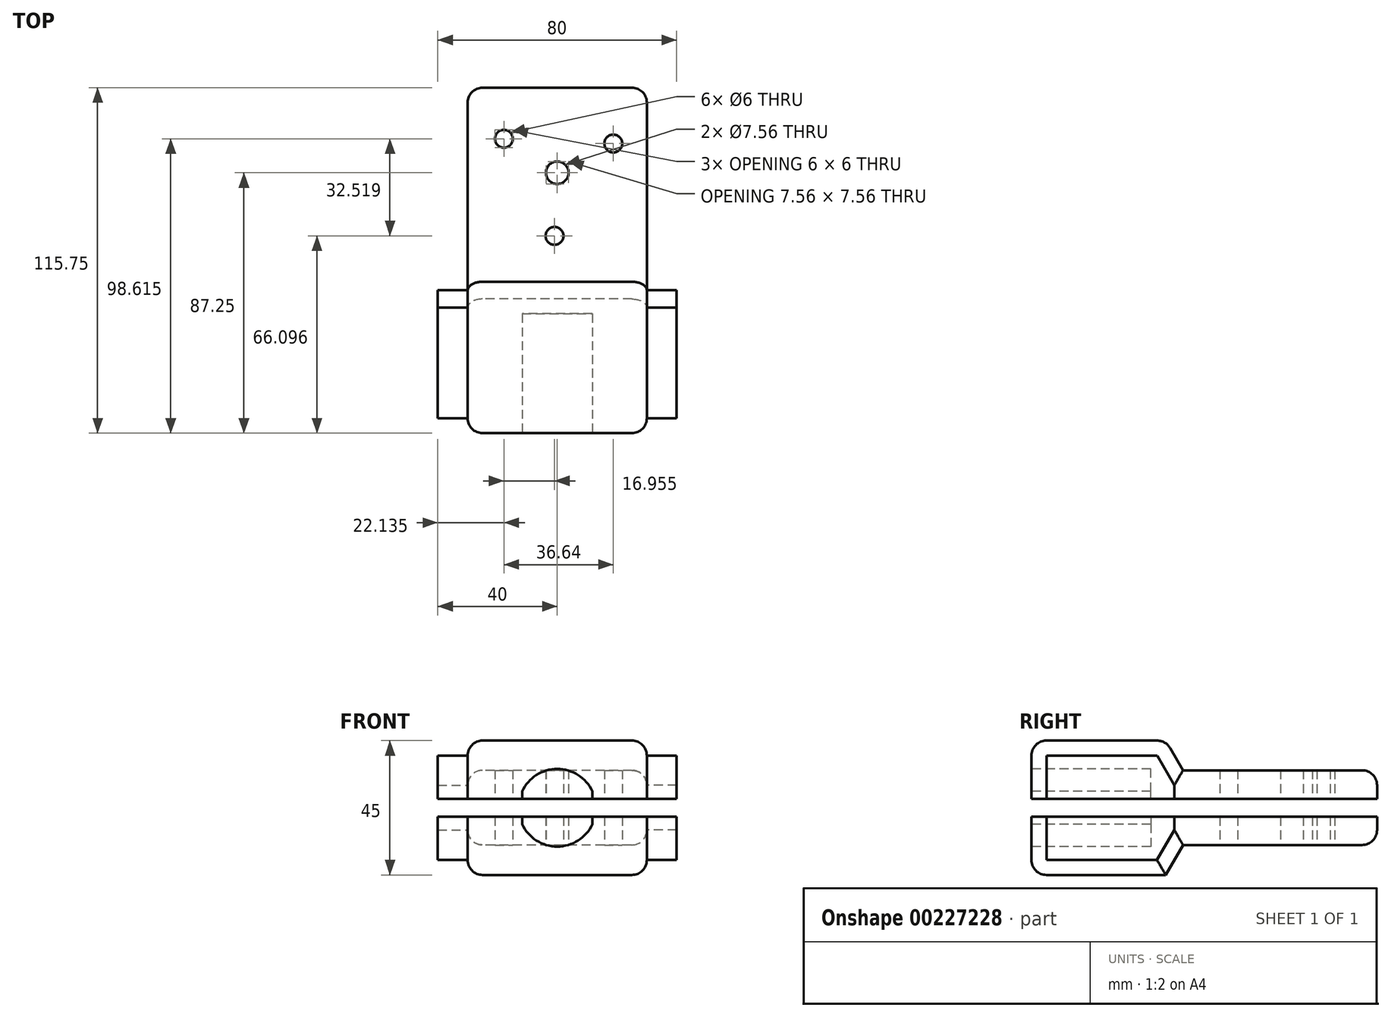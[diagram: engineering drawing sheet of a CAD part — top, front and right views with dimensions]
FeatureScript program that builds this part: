
annotation { "Feature Type Name" : "Feature", "Feature Type Description" : "" }
export const myFeature = defineFeature(function(context is Context, id is Id, definition is map)
    precondition{}
    {
        {
            var Q0;
            Q0=qCreatedBy(makeId("Right.planeOp"),FACE);
            var sketch = newSketch(context, id + "F0", { "sketchPlane" : qUnion([Q0])});
            skLineSegment(sketch, "E0", {"start": v(-50.75, 9.96) * mm, "end": v(-5.75, 9.96) * mm});
            skLineSegment(sketch, "E1", {"start": v(65, 0) * mm, "end": v(65, -25) * mm});
            skLineSegment(sketch, "E2", {"start": v(65, -25) * mm, "end": v(0, -25) * mm});
            skLineSegment(sketch, "E3", {"start": v(0, -25) * mm, "end": v(-5.8, -35.04) * mm});
            skLineSegment(sketch, "E4", {"start": v(-5.8, -35.04) * mm, "end": v(-50.75, -35.04) * mm});
            skLineSegment(sketch, "E5", {"start": v(-50.75, -35.04) * mm, "end": v(-50.75, 9.96) * mm});
            skLineSegment(sketch, "E6", {"start": v(0, 0) * mm, "end": v(-5.75, 9.96) * mm});
            skLineSegment(sketch, "E7", {"start": v(0, 0) * mm, "end": v(65, 0) * mm});
            skSolve(sketch);
        }
        {
            var Q0;
            Q0 = qSketchRegion(id + "F0", true);
            extrude(context, id + "F1", {"entities" : qUnion([Q0]), "endBound" : BoundingType.SYMMETRIC, "depth" : 60 * mm});
        }
        {
            var Q0;
            Q0=makeQuery(id+"F1.opExtrude","SWEPT_FACE",FACE,{"disambiguationData":[OSD([sQuery(id+"F0.wireOp",EDGE,"E5")])]});
            var sketch = newSketch(context, id + "F2", { "sketchPlane" : qUnion([Q0])});
            skLineSegment(sketch, "E8", {"start": v(0, -35.04) * mm, "end": v(0, 9.96) * mm, "construction": true});
            skCircle(sketch, "E9", {"center": v(0, -12.54) * mm, "radius": 13 * mm});
            skSolve(sketch);
        }
        {
            var Q0;
            Q0 = qSketchRegion(id + "F2", true);
            extrude(context, id + "F3", {"entities" : qUnion([Q0]), "operationType" : NewBodyOperationType.REMOVE, "oppositeDirection" : true, "depth" : 40 * mm});
        }
        {
            var Q0;
            Q0=makeQuery(id+"F1.opExtrude","SWEPT_EDGE",EDGE,{"disambiguationData":[OSD([sQuery(id+"F0.wireOp",EDGE,"E1"),sQuery(id+"F0.wireOp",EDGE,"E7")])]});
            var Q1;
            Q1=makeQuery(id+"F1.opExtrude","SWEPT_EDGE",EDGE,{"disambiguationData":[OSD([sQuery(id+"F0.wireOp",EDGE,"E1"),sQuery(id+"F0.wireOp",EDGE,"E2")])]});
            var Q2;
            Q2=makeQuery(id+"F1.opExtrude","CAP_EDGE",EDGE,{"disambiguationData":[OSD([sQuery(id+"F0.wireOp",EDGE,"E1")])],"isStart":true});
            var Q3;
            Q3=makeQuery(id+"F1.opExtrude","CAP_EDGE",EDGE,{"disambiguationData":[OSD([sQuery(id+"F0.wireOp",EDGE,"E1")])],"isStart":false});
            var Q4;
            Q4=makeQuery(id+"F1.opExtrude","CAP_EDGE",EDGE,{"disambiguationData":[OSD([sQuery(id+"F0.wireOp",EDGE,"E7")])],"isStart":false});
            var Q5;
            Q5=makeQuery(id+"F1.opExtrude","CAP_EDGE",EDGE,{"disambiguationData":[OSD([sQuery(id+"F0.wireOp",EDGE,"E2")])],"isStart":false});
            var Q6;
            Q6=makeQuery(id+"F1.opExtrude","CAP_EDGE",EDGE,{"disambiguationData":[OSD([sQuery(id+"F0.wireOp",EDGE,"E2")])],"isStart":true});
            var Q7;
            Q7=makeQuery(id+"F1.opExtrude","CAP_EDGE",EDGE,{"disambiguationData":[OSD([sQuery(id+"F0.wireOp",EDGE,"E7")])],"isStart":true});
            var Q8;
            Q8=makeQuery(id+"F1.opExtrude","SWEPT_EDGE",EDGE,{"disambiguationData":[OSD([sQuery(id+"F0.wireOp",EDGE,"E0"),sQuery(id+"F0.wireOp",EDGE,"E6")])]});
            var Q9;
            Q9=makeQuery(id+"F1.opExtrude","CAP_EDGE",EDGE,{"disambiguationData":[OSD([sQuery(id+"F0.wireOp",EDGE,"E0")])],"isStart":false});
            var Q10;
            Q10=makeQuery(id+"F1.opExtrude","SWEPT_EDGE",EDGE,{"disambiguationData":[OSD([sQuery(id+"F0.wireOp",EDGE,"E0"),sQuery(id+"F0.wireOp",EDGE,"E5")])]});
            var Q11;
            Q11=makeQuery(id+"F1.opExtrude","CAP_EDGE",EDGE,{"disambiguationData":[OSD([sQuery(id+"F0.wireOp",EDGE,"E0")])],"isStart":true});
            var Q12;
            Q12=makeQuery(id+"F1.opExtrude","CAP_EDGE",EDGE,{"disambiguationData":[OSD([sQuery(id+"F0.wireOp",EDGE,"E6")])],"isStart":false});
            var Q13;
            Q13=makeQuery(id+"F1.opExtrude","CAP_EDGE",EDGE,{"disambiguationData":[OSD([sQuery(id+"F0.wireOp",EDGE,"E6")])],"isStart":true});
            var Q14;
            Q14=makeQuery(id+"F1.opExtrude","CAP_EDGE",EDGE,{"disambiguationData":[OSD([sQuery(id+"F0.wireOp",EDGE,"E3")])],"isStart":false});
            var Q15;
            Q15=makeQuery(id+"F1.opExtrude","CAP_EDGE",EDGE,{"disambiguationData":[OSD([sQuery(id+"F0.wireOp",EDGE,"E3")])],"isStart":true});
            var Q16;
            Q16=makeQuery(id+"F1.opExtrude","CAP_EDGE",EDGE,{"disambiguationData":[OSD([sQuery(id+"F0.wireOp",EDGE,"E4")])],"isStart":false});
            var Q17;
            Q17=makeQuery(id+"F1.opExtrude","CAP_EDGE",EDGE,{"disambiguationData":[OSD([sQuery(id+"F0.wireOp",EDGE,"E4")])],"isStart":true});
            var Q18;
            Q18=makeQuery(id+"F1.opExtrude","SWEPT_EDGE",EDGE,{"disambiguationData":[OSD([sQuery(id+"F0.wireOp",EDGE,"E4"),sQuery(id+"F0.wireOp",EDGE,"E5")])]});
            var Q19;
            Q19=makeQuery(id+"F1.opExtrude","CAP_EDGE",EDGE,{"disambiguationData":[OSD([sQuery(id+"F0.wireOp",EDGE,"E5")])],"isStart":false});
            var Q20;
            Q20=makeQuery(id+"F1.opExtrude","CAP_EDGE",EDGE,{"disambiguationData":[OSD([sQuery(id+"F0.wireOp",EDGE,"E5")])],"isStart":true});
            fillet(context, id + "F4", {"entities" : qUnion([Q0, Q1, Q2, Q3, Q4, Q5, Q6, Q7, Q8, Q9, Q10, Q11, Q12, Q13, Q14, Q15, Q16, Q17, Q18, Q19, Q20]), "radius" : 5 * mm, "tangentPropagation" : true, "allowEdgeOverflow" : false});
        }
        {
            var Q0;
            Q0=makeQuery(id+"F1.opExtrude","SWEPT_FACE",FACE,{"disambiguationData":[OSD([sQuery(id+"F0.wireOp",EDGE,"E2")])]});
            var sketch = newSketch(context, id + "F5", { "sketchPlane" : qUnion([Q0])});
            skCircle(sketch, "E10", {"center": v(-17.86, -47.86) * mm, "radius": 3 * mm});
            skCircle(sketch, "E11.1.0", {"center": v(18.77, -46.29) * mm, "radius": 3 * mm});
            skCircle(sketch, "E11.2.0", {"center": v(-0.9, -15.35) * mm, "radius": 3 * mm});
            skPoint(sketch, "E11.center", {"position": v(0, -36.5) * mm});
            skCircle(sketch, "E12", {"center": v(0, -36.5) * mm, "radius": 3.78 * mm});
            skSolve(sketch);
        }
        {
            var Q0;
            Q0 = qSketchRegion(id + "F5", true);
            extrude(context, id + "F6", {"entities" : qUnion([Q0]), "operationType" : NewBodyOperationType.REMOVE, "oppositeDirection" : true, "depth" : 39.9 * mm});
        }
        {
            var Q0;
            Q0=makeQuery(id+"F1.opExtrude","SWEPT_FACE",FACE,{"disambiguationData":[OSD([sQuery(id+"F0.wireOp",EDGE,"E5")])]});
            var sketch = newSketch(context, id + "F7", { "sketchPlane" : qUnion([Q0])});
            skLineSegment(sketch, "E13", {"start": v(-25, -7.04) * mm, "end": v(25, -7.04) * mm});
            skLineSegment(sketch, "E14", {"start": v(25, -7.04) * mm, "end": v(25, -18.04) * mm});
            skLineSegment(sketch, "E15", {"start": v(25, -18.04) * mm, "end": v(-25, -18.04) * mm});
            skLineSegment(sketch, "E16", {"start": v(-25, -18.04) * mm, "end": v(-25, -7.04) * mm});
            skLineSegment(sketch, "E17", {"start": v(-25, -7.04) * mm, "end": v(-35.45, -7.04) * mm});
            skLineSegment(sketch, "E18", {"start": v(-35.45, -7.04) * mm, "end": v(-35.45, -18.04) * mm});
            skLineSegment(sketch, "E19", {"start": v(-35.45, -18.04) * mm, "end": v(-25, -18.04) * mm});
            skLineSegment(sketch, "E20", {"start": v(25, -7.04) * mm, "end": v(35.45, -7.04) * mm});
            skLineSegment(sketch, "E21", {"start": v(35.45, -7.04) * mm, "end": v(35.45, -18.04) * mm});
            skLineSegment(sketch, "E22", {"start": v(35.45, -18.04) * mm, "end": v(25, -18.04) * mm});
            skSolve(sketch);
        }
        {
            var Q0;
            Q0 = qSketchRegion(id + "F7", true);
            extrude(context, id + "F8", {"entities" : qUnion([Q0]), "operationType" : NewBodyOperationType.REMOVE, "oppositeDirection" : true, "depth" : 159.3 * mm});
        }
        {
            var Q0;
            Q0=makeQuery(id+"F1.opExtrude","CAP_FACE",FACE,{"disambiguationData":[OSD([sQuery(id+"F0.wireOp",EDGE,"E0"),sQuery(id+"F0.wireOp",EDGE,"E1"),sQuery(id+"F0.wireOp",EDGE,"E2"),sQuery(id+"F0.wireOp",EDGE,"E3"),sQuery(id+"F0.wireOp",EDGE,"E4"),sQuery(id+"F0.wireOp",EDGE,"E5"),sQuery(id+"F0.wireOp",EDGE,"E6"),sQuery(id+"F0.wireOp",EDGE,"E7")])],"isStart":false});
            extrude(context, id + "F9", {"entities" : qUnion([Q0]), "operationType" : NewBodyOperationType.ADD, "depth" : 10 * mm});
        }
        {
            var Q0;
            {var subQ0=sQuery(id+"F0.wireOp",EDGE,"E7");var subQ1=sQuery(id+"F0.wireOp",EDGE,"E6");var subQ2=sQuery(id+"F0.wireOp",EDGE,"E5");var subQ3=sQuery(id+"F0.wireOp",EDGE,"E4");var subQ4=sQuery(id+"F0.wireOp",EDGE,"E3");var subQ5=sQuery(id+"F0.wireOp",EDGE,"E2");var subQ6=sQuery(id+"F0.wireOp",EDGE,"E1");var subQ7=sQuery(id+"F0.wireOp",EDGE,"E0");Q0=makeQuery(id+"F9.opExtrude","SWEPT_FACE",FACE,{"disambiguationData":[OSD([subQ7,subQ6,subQ5,subQ4,subQ3,subQ2,subQ1,subQ0]),TDD([makeQuery(id+"F4.opFillet","BLEND_EDGE",EDGE,{"blendedFrom":[makeQuery(id+"F1.opExtrude","CAP_EDGE",EDGE,{"disambiguationData":[OSD([subQ0])],"isStart":false}),makeQuery(id+"F1.opExtrude","CAP_FACE",FACE,{"disambiguationData":[OSD([subQ7,subQ6,subQ5,subQ4,subQ3,subQ2,subQ1,subQ0])],"isStart":false})],"blendedInto":[makeQuery(id+"F1.opExtrude","CAP_FACE",FACE,{"disambiguationData":[OSD([subQ7,subQ6,subQ5,subQ4,subQ3,subQ2,subQ1,subQ0])],"isStart":false})]})])]});}
            extrude(context, id + "F10", {"entities" : qUnion([Q0]), "operationType" : NewBodyOperationType.REMOVE, "oppositeDirection" : true, "depth" : 25 * mm});
        }
        {
            var Q0;
            Q0=makeQuery(id+"F1.opExtrude","CAP_FACE",FACE,{"disambiguationData":[OSD([sQuery(id+"F0.wireOp",EDGE,"E0"),sQuery(id+"F0.wireOp",EDGE,"E1"),sQuery(id+"F0.wireOp",EDGE,"E2"),sQuery(id+"F0.wireOp",EDGE,"E3"),sQuery(id+"F0.wireOp",EDGE,"E4"),sQuery(id+"F0.wireOp",EDGE,"E5"),sQuery(id+"F0.wireOp",EDGE,"E6"),sQuery(id+"F0.wireOp",EDGE,"E7")])],"isStart":true});
            extrude(context, id + "F11", {"entities" : qUnion([Q0]), "operationType" : NewBodyOperationType.ADD, "depth" : 10 * mm});
        }
        {
            var Q0;
            {var subQ0=sQuery(id+"F0.wireOp",EDGE,"E7");var subQ1=sQuery(id+"F0.wireOp",EDGE,"E6");var subQ2=sQuery(id+"F0.wireOp",EDGE,"E5");var subQ3=sQuery(id+"F0.wireOp",EDGE,"E4");var subQ4=sQuery(id+"F0.wireOp",EDGE,"E3");var subQ5=sQuery(id+"F0.wireOp",EDGE,"E2");var subQ6=sQuery(id+"F0.wireOp",EDGE,"E1");var subQ7=sQuery(id+"F0.wireOp",EDGE,"E0");Q0=makeQuery(id+"F11.opExtrude","SWEPT_FACE",FACE,{"disambiguationData":[OSD([subQ7,subQ6,subQ5,subQ4,subQ3,subQ2,subQ1,subQ0]),TDD([makeQuery(id+"F4.opFillet","BLEND_EDGE",EDGE,{"blendedFrom":[makeQuery(id+"F1.opExtrude","CAP_EDGE",EDGE,{"disambiguationData":[OSD([subQ0])],"isStart":true}),makeQuery(id+"F1.opExtrude","CAP_FACE",FACE,{"disambiguationData":[OSD([subQ7,subQ6,subQ5,subQ4,subQ3,subQ2,subQ1,subQ0])],"isStart":true})],"blendedInto":[makeQuery(id+"F1.opExtrude","CAP_FACE",FACE,{"disambiguationData":[OSD([subQ7,subQ6,subQ5,subQ4,subQ3,subQ2,subQ1,subQ0])],"isStart":true})]})])]});}
            extrude(context, id + "F12", {"entities" : qUnion([Q0]), "operationType" : NewBodyOperationType.REMOVE, "oppositeDirection" : true, "depth" : 25 * mm});
        }
        {
            var Q0;
            {var subQ0=sQuery(id+"F7.wireOp",EDGE,"E20");var subQ1=sQuery(id+"F7.wireOp",EDGE,"E17");var subQ2=sQuery(id+"F7.wireOp",EDGE,"E13");var subQ3=sQuery(id+"F0.wireOp",EDGE,"E7");var subQ4=sQuery(id+"F0.wireOp",EDGE,"E6");var subQ5=sQuery(id+"F0.wireOp",EDGE,"E5");var subQ6=sQuery(id+"F0.wireOp",EDGE,"E4");var subQ7=sQuery(id+"F0.wireOp",EDGE,"E3");var subQ8=sQuery(id+"F0.wireOp",EDGE,"E2");var subQ9=sQuery(id+"F0.wireOp",EDGE,"E1");var subQ10=sQuery(id+"F0.wireOp",EDGE,"E0");Q0=makeQuery(id+"F11.boolean.opBoolean","MERGE",FACE,{"derivedFrom":[makeQuery(id+"F9.boolean.opBoolean","MERGE",FACE,{"derivedFrom":[makeQuery(id+"F8.boolean.opBoolean","COPY",FACE,{"derivedFrom":makeQuery(id+"F8.opExtrude","SWEPT_FACE",FACE,{"disambiguationData":[OSD([subQ2,subQ1,subQ0])]})}),makeQuery(id+"F9.opExtrude","SWEPT_FACE",FACE,{"disambiguationData":[OSD([subQ10,subQ9,subQ8,subQ7,subQ6,subQ5,subQ4,subQ3,subQ2,subQ1,subQ0])]})]}),makeQuery(id+"F11.opExtrude","SWEPT_FACE",FACE,{"disambiguationData":[OSD([subQ10,subQ9,subQ8,subQ7,subQ6,subQ5,subQ4,subQ3,subQ2,subQ1,subQ0])]})]});}
            extrude(context, id + "F13", {"entities" : qUnion([Q0]), "operationType" : NewBodyOperationType.ADD, "depth" : 2.5 * mm});
        }
        {
            var Q0;
            {var subQ0=sQuery(id+"F7.wireOp",EDGE,"E22");var subQ1=sQuery(id+"F7.wireOp",EDGE,"E19");var subQ2=sQuery(id+"F7.wireOp",EDGE,"E15");var subQ3=sQuery(id+"F0.wireOp",EDGE,"E7");var subQ4=sQuery(id+"F0.wireOp",EDGE,"E6");var subQ5=sQuery(id+"F0.wireOp",EDGE,"E5");var subQ6=sQuery(id+"F0.wireOp",EDGE,"E4");var subQ7=sQuery(id+"F0.wireOp",EDGE,"E3");var subQ8=sQuery(id+"F0.wireOp",EDGE,"E2");var subQ9=sQuery(id+"F0.wireOp",EDGE,"E1");var subQ10=sQuery(id+"F0.wireOp",EDGE,"E0");Q0=makeQuery(id+"F11.boolean.opBoolean","MERGE",FACE,{"derivedFrom":[makeQuery(id+"F9.boolean.opBoolean","MERGE",FACE,{"derivedFrom":[makeQuery(id+"F8.boolean.opBoolean","COPY",FACE,{"derivedFrom":makeQuery(id+"F8.opExtrude","SWEPT_FACE",FACE,{"disambiguationData":[OSD([subQ2,subQ1,subQ0])]})}),makeQuery(id+"F9.opExtrude","SWEPT_FACE",FACE,{"disambiguationData":[OSD([subQ10,subQ9,subQ8,subQ7,subQ6,subQ5,subQ4,subQ3,subQ2,subQ1,subQ0])]})]}),makeQuery(id+"F11.opExtrude","SWEPT_FACE",FACE,{"disambiguationData":[OSD([subQ10,subQ9,subQ8,subQ7,subQ6,subQ5,subQ4,subQ3,subQ2,subQ1,subQ0])]})]});}
            extrude(context, id + "F14", {"entities" : qUnion([Q0]), "operationType" : NewBodyOperationType.ADD, "depth" : 2.5 * mm});
        }
    });
